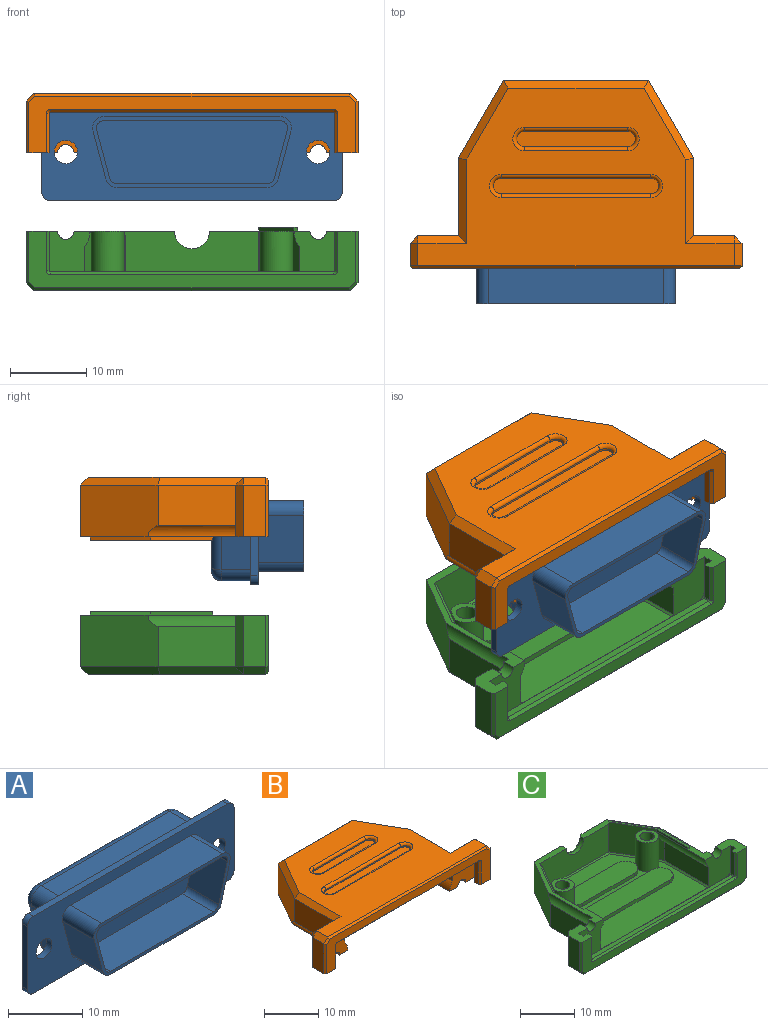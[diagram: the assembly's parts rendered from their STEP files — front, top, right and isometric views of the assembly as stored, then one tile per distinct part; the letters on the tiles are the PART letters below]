
ASSEMBLY  parts=3 mates=2
PART A: 47 faces, bbox 39.4x12.1x12.7 mm
  f0: plane 39.37x12.7mm, normal (0,1,0), area 180.2mm2, adj f2,f3,f4,f5,f6,f7,f8,f9
  f1: plane 39.37x12.7mm, normal (0,-1,0), area 260mm2, adj f2,f3,f4,f5,f6,f7,f8,f9
  f2: plane 10.41x1.02mm, normal (1,0,0), area 10.6mm2, adj f0,f1,f3,f11
  f3: cylinder r=1.14mm len=1.14mm, axis (0,-1,0), area 1.8mm2, adj f0,f1,f2,f4
  f4: plane 37.08x1.02mm, normal (0,0,1), area 37.7mm2, adj f0,f1,f3,f5
  f5: cylinder r=1.14mm len=1.14mm, axis (0,-1,0), area 1.8mm2, adj f0,f1,f4,f6
  f6: plane 10.41x1.02mm, normal (-1,0,0), area 10.6mm2, adj f0,f1,f5,f7
  f7: cylinder r=1.14mm len=1.14mm, axis (0,-1,0), area 1.8mm2, adj f0,f1,f6,f8
  f8: plane 37.08x1.02mm, normal (0,0,-1), area 37.7mm2, adj f0,f1,f7,f11
  f9: cylinder r=1.52mm len=3.05mm, axis (0,-1,0), area 9.7mm2, adj f0,f1
  f10: cylinder r=1.52mm len=3.05mm, axis (0,-1,0), area 9.7mm2, adj f0,f1
  f11: cylinder r=1.14mm len=1.14mm, axis (0,-1,0), area 1.8mm2, adj f0,f1,f2,f8
  f12: plane 6.22x5.97mm, normal (0.97,0,-0.26), area 38.5mm2, adj f1,f13,f27,f28
  f13: cylinder r=1.52mm len=5.97mm, axis (0,1,0), area 16.7mm2, adj f1,f12,f14,f28
  f14: plane 22.95x5.97mm, normal (0,0,1), area 137mm2, adj f1,f13,f15,f28
  f15: cylinder r=1.52mm len=5.97mm, axis (0,1,0), area 16.7mm2, adj f1,f14,f16,f28
  f16: plane 6.22x5.97mm, normal (-0.97,0,-0.26), area 38.5mm2, adj f1,f15,f17,f28
  f17: cylinder r=1.52mm len=5.97mm, axis (0,1,0), area 11.9mm2, adj f1,f16,f18,f28
  f18: plane 19.62x5.97mm, normal (0,0,-1), area 117.1mm2, adj f1,f17,f27,f28
  f19: cylinder r=1.02mm len=5.97mm, axis (0,1,0), area 11.1mm2, adj f20,f26,f28,f29
  f20: plane 6.22x5.97mm, normal (-0.97,0,0.26), area 38.5mm2, adj f19,f21,f28,f29
  f21: cylinder r=1.02mm len=5.97mm, axis (0,1,0), area 7.9mm2, adj f20,f22,f28,f29
  f22: plane 19.62x5.97mm, normal (0,0,1), area 117.1mm2, adj f21,f23,f28,f29
  f23: cylinder r=1.02mm len=5.97mm, axis (0,1,0), area 7.9mm2, adj f22,f24,f28,f29
  f24: plane 6.22x5.97mm, normal (0.97,0,0.26), area 38.5mm2, adj f23,f25,f28,f29
  f25: cylinder r=1.02mm len=5.97mm, axis (0,1,0), area 11.1mm2, adj f24,f26,f28,f29
  f26: plane 22.95x5.97mm, normal (0,0,-1), area 137mm2, adj f19,f25,f28,f29
  f27: cylinder r=1.52mm len=5.97mm, axis (0,1,0), area 11.9mm2, adj f1,f12,f18,f28
  f28: plane 26x9.27mm, normal (0,-1,0), area 32.2mm2, adj f12,f13,f14,f15,f16,f17,f18,f19
  f29: plane 24.98x8.26mm, normal (0,-1,0), area 192mm2, adj f19,f20,f21,f22,f23,f24,f25,f26
  f30: plane 7.87x3.81mm, normal (-0.97,0,-0.26), area 31.1mm2, adj f0,f31,f37,f42
  f31: cylinder r=1.91mm len=3.81mm, axis (0,-1,0), area 13.3mm2, adj f0,f30,f32,f40
  f32: plane 24.5x3.81mm, normal (0,0,1), area 93.3mm2, adj f0,f31,f33,f39
  f33: cylinder r=1.91mm len=3.81mm, axis (0,-1,0), area 13.3mm2, adj f0,f32,f34,f41
  f34: plane 7.87x3.81mm, normal (0.97,0,-0.26), area 31.1mm2, adj f0,f33,f35,f43
  f35: cylinder r=1.91mm len=3.81mm, axis (0,-1,0), area 9.5mm2, adj f0,f34,f36,f45
  f36: plane 20.28x3.81mm, normal (0,0,-1), area 77.3mm2, adj f0,f35,f37,f46
  f37: cylinder r=1.91mm len=3.81mm, axis (0,-1,0), area 9.5mm2, adj f0,f30,f36,f44
  f38: plane 25.77x9.14mm, normal (0,1,0), area 216.3mm2, adj f39,f40,f41,f42,f43,f44,f45,f46
  f39: cylinder r=1.27mm len=24.5mm, axis (-1,0,0), area 48.9mm2, adj f32,f38,f40,f41
  f40: torus R=0.64mm, axis (0,1,0), area 5.3mm2, adj f31,f38,f39,f42
  f41: torus R=0.64mm, axis (0,1,0), area 5.3mm2, adj f33,f38,f39,f43
  f42: cylinder r=1.27mm len=8.2mm, axis (0.26,0,-0.97), area 16.3mm2, adj f30,f38,f40,f44
  f43: cylinder r=1.27mm len=8.2mm, axis (0.26,0,0.97), area 16.3mm2, adj f34,f38,f41,f45
  f44: torus R=0.64mm, axis (0,1,0), area 3.8mm2, adj f37,f38,f42,f46
  f45: torus R=0.64mm, axis (0,1,0), area 3.8mm2, adj f35,f38,f43,f46
  f46: cylinder r=1.27mm len=20.28mm, axis (1,0,0), area 40.5mm2, adj f36,f38,f44,f45
PART B: 123 faces, bbox 43.4x24.6x8.3 mm
  f0: cone r=0mm half-angle=59deg, axis (0,0,-1), area 3.6mm2, adj f117,f122
  f1: cone r=0mm half-angle=59deg, axis (0,0,-1), area 3.6mm2, adj f118,f120
  f2: plane 22.1x13.14mm, normal (0,0,-1), area 30.9mm2, adj f3,f4,f17,f22,f60,f63,f76,f83
  f3: plane 39.88x6.6mm, normal (0,-1,0), area 77.1mm2, adj f2,f8,f10,f13,f14,f15,f27,f28
  f4: plane 18.99x6.78mm, normal (0,1,0), area 116.5mm2, adj f2,f13,f21,f22,f43,f116
  f5: plane 5.75x1.53mm, normal (-0.87,-0.5,0), area 8.8mm2, adj f8,f11,f75,f95,f106
  f6: plane 4.32x4.32mm, normal (0,0,-1), area 8.7mm2, adj f95,f102,f118
  f7: plane 5.94x5.75mm, normal (-0.87,-0.5,0), area 39.4mm2, adj f76,f81,f95,f106
  f8: cylinder r=3.17mm len=12.83mm, axis (0,-1,0), area 23.7mm2, adj f3,f5,f13,f75,f103,f106
  f9: plane 4.32x4.32mm, normal (0,0,-1), area 8.7mm2, adj f77,f94,f117
  f10: plane 27.63x20.56mm, normal (0,0,-1), area 309.5mm2, adj f3,f11,f12,f78,f79,f80,f81,f82
  f11: plane 1.6x0.92mm, normal (-0.61,-0.35,-0.71), area 0.6mm2, adj f5,f10,f82,f95
  f12: plane 1.6x0.92mm, normal (0.61,-0.35,-0.71), area 0.6mm2, adj f10,f77,f78,f94
  f13: plane 22.1x13.14mm, normal (0,0,-1), area 30.9mm2, adj f3,f4,f8,f16,f21,f61,f62,f76
  f14: plane 4.32x4.13mm, normal (0,0,-1), area 12.8mm2, adj f3,f17,f19,f23,f24,f27,f32,f38
  f15: plane 4.32x4.13mm, normal (0,0,-1), area 12.8mm2, adj f3,f16,f19,f24,f25,f28,f33,f49
  f16: plane 6.78x6.1mm, normal (0,1,0), area 35.2mm2, adj f13,f15,f20,f47,f49,f61,f62
  f17: plane 6.78x6.1mm, normal (0,1,0), area 35.2mm2, adj f2,f14,f18,f38,f40,f60,f63
  f18: plane 10.16x5.26mm, normal (-1,0,0), area 53.5mm2, adj f17,f22,f41,f60
  f19: plane 39.88x6.6mm, normal (0,1,0), area 63.4mm2, adj f14,f15,f27,f28,f29,f30,f31,f32
  f20: plane 10.16x5.26mm, normal (1,0,0), area 53.5mm2, adj f16,f21,f45,f61
  f21: plane 10.16x6.78mm, normal (0.87,0.5,0), area 78mm2, adj f4,f13,f20,f44,f61
  f22: plane 10.16x6.78mm, normal (-0.87,0.5,0), area 78mm2, adj f2,f4,f18,f42,f60
  f23: plane 6.78x2.92mm, normal (-1,0,0), area 19.8mm2, adj f14,f37,f38,f59
  f24: plane 42.67x7.42mm, normal (0,-1,0), area 98.2mm2, adj f14,f15,f50,f51,f52,f53,f54,f55
  f25: plane 6.78x2.92mm, normal (1,0,0), area 19.8mm2, adj f15,f46,f49,f55
  f26: plane 41.4x23.24mm, normal (0,0,1), area 537.1mm2, adj f37,f40,f41,f42,f43,f44,f45,f46
  f27: plane 5.21x1.27mm, normal (1,0,0), area 6.6mm2, adj f3,f14,f19,f31
  f28: plane 5.21x1.27mm, normal (-1,0,0), area 6.6mm2, adj f3,f15,f19,f29
  f29: cylinder r=1.4mm len=1.4mm, axis (0,-1,0), area 2.8mm2, adj f3,f19,f28,f30
  f30: plane 37.08x1.27mm, normal (0,0,-1), area 47.1mm2, adj f3,f19,f29,f31
  f31: cylinder r=1.4mm len=1.4mm, axis (0,-1,0), area 2.8mm2, adj f3,f19,f27,f30
  f32: plane 5.21x0.89mm, normal (1,0,0), area 4.6mm2, adj f14,f19,f36,f54
  f33: plane 5.21x0.89mm, normal (-1,0,0), area 4.6mm2, adj f15,f19,f34,f50
  f34: cylinder r=0.13mm len=0.89mm, axis (0,1,0), area 0.2mm2, adj f19,f33,f35,f51
  f35: plane 37.08x0.89mm, normal (0,0,-1), area 33mm2, adj f19,f34,f36,f52
  f36: cylinder r=0.13mm len=0.89mm, axis (0,1,0), area 0.2mm2, adj f19,f32,f35,f53
  f37: plane 2.92x1.02mm, normal (-0.71,0,0.71), area 4.2mm2, adj f23,f26,f39,f58
  f38: plane 6.78x1.02mm, normal (-0.71,0.71,0), area 9.7mm2, adj f14,f17,f23,f39
  f39: plane 1.02x1.02mm, normal (-0.58,0.58,0.58), area 0.9mm2, adj f37,f38,f40
  f40: plane 6.36x1.02mm, normal (0,0.71,0.71), area 8.4mm2, adj f17,f26,f39,f41
  f41: plane 11.18x1.02mm, normal (-0.71,0,0.71), area 15.1mm2, adj f18,f26,f40,f42
  f42: plane 10.43x6.45mm, normal (-0.61,0.35,0.71), area 16.2mm2, adj f22,f26,f41,f43
  f43: plane 18.99x1.02mm, normal (0,0.71,0.71), area 26.4mm2, adj f4,f26,f42,f44
  f44: plane 10.43x6.45mm, normal (0.61,0.35,0.71), area 16.2mm2, adj f21,f26,f43,f45
  f45: plane 11.18x1.02mm, normal (0.71,0,0.71), area 15.1mm2, adj f20,f26,f44,f47
  f46: plane 2.92x1.02mm, normal (0.71,0,0.71), area 4.2mm2, adj f25,f26,f48,f56
  f47: plane 6.36x1.02mm, normal (0,0.71,0.71), area 8.4mm2, adj f16,f26,f45,f48
  f48: plane 1.02x1.02mm, normal (0.58,0.58,0.58), area 0.9mm2, adj f46,f47,f49
  f49: plane 6.78x1.02mm, normal (0.71,0.71,0), area 9.7mm2, adj f15,f16,f25,f48
  f50: plane 5.21x0.38mm, normal (-0.71,-0.71,0), area 2.8mm2, adj f15,f24,f33,f51
  f51: cone r=0.51mm half-angle=45deg, axis (0,-1,0), area 0.3mm2, adj f24,f34,f50,f52
  f52: plane 37.08x0.38mm, normal (0,-0.71,-0.71), area 20mm2, adj f24,f35,f51,f53
  f53: cone r=0.51mm half-angle=45deg, axis (0,-1,0), area 0.3mm2, adj f24,f36,f52,f54
  f54: plane 5.21x0.38mm, normal (0.71,-0.71,0), area 2.8mm2, adj f14,f24,f32,f53
  f55: plane 6.78x0.38mm, normal (0.71,-0.71,0), area 3.6mm2, adj f15,f24,f25,f56
  f56: plane 1.17x1.17mm, normal (0.5,-0.71,0.5), area 0.7mm2, adj f24,f46,f55,f57
  f57: plane 41.4x0.38mm, normal (0,-0.71,0.71), area 22.2mm2, adj f24,f26,f56,f58
  f58: plane 1.17x1.17mm, normal (-0.5,-0.71,0.5), area 0.7mm2, adj f24,f37,f57,f59
  f59: plane 6.78x0.38mm, normal (-0.71,-0.71,0), area 3.6mm2, adj f14,f23,f24,f58
  f60: cylinder r=1.91mm len=11.47mm, axis (0,-1,0), area 19.4mm2, adj f2,f17,f18,f22
  f61: cylinder r=1.91mm len=11.47mm, axis (0,-1,0), area 19.4mm2, adj f13,f16,f20,f21
  f62: cylinder r=1.08mm len=2.16mm, axis (0,1,0), area 6mm2, adj f3,f13,f15,f16
  f63: cylinder r=1.08mm len=2.16mm, axis (0,1,0), area 6mm2, adj f2,f3,f14,f17
  f64: plane 19.62x0.25mm, normal (0,-1,0), area 5mm2, adj f65,f67,f68,f108
  f65: cylinder r=1.02mm len=2.03mm, axis (0,0,1), area 0.8mm2, adj f64,f66,f68,f109
  f66: plane 19.62x0.25mm, normal (0,1,0), area 5mm2, adj f65,f67,f68,f111
  f67: cylinder r=1.02mm len=2.03mm, axis (0,0,1), area 0.8mm2, adj f64,f66,f68,f110
  f68: plane 21.65x2.03mm, normal (0,0,1), area 43.1mm2, adj f64,f65,f66,f67
  f69: plane 13.5x0.25mm, normal (0,-1,0), area 3.4mm2, adj f70,f72,f73,f112
  f70: cylinder r=1.02mm len=2.03mm, axis (0,0,1), area 0.8mm2, adj f69,f71,f73,f113
  f71: plane 13.5x0.25mm, normal (0,1,0), area 3.4mm2, adj f70,f72,f73,f115
  f72: cylinder r=1.02mm len=2.03mm, axis (0,0,1), area 0.8mm2, adj f69,f71,f73,f114
  f73: plane 15.53x2.03mm, normal (0,0,1), area 30.7mm2, adj f69,f70,f71,f72
  f74: plane 11.6x4.2mm, normal (1,0,0), area 48.7mm2, adj f3,f77,f78,f83
  f75: plane 11.6x4.2mm, normal (-1,0,0), area 48.7mm2, adj f3,f5,f8,f82
  f76: plane 18.03x6.26mm, normal (0,-1,0), area 101.7mm2, adj f2,f7,f13,f77,f80,f104,f106,f107
  f77: plane 9.23x6.76mm, normal (0.87,-0.5,0), area 56.5mm2, adj f9,f12,f74,f76,f79,f83,f94,f96
  f78: plane 11.6x0.27mm, normal (0.71,0,-0.71), area 4.4mm2, adj f3,f10,f12,f74
  f79: plane 5.94x3.59mm, normal (0.61,-0.35,-0.71), area 2.5mm2, adj f10,f77,f80,f94
  f80: plane 17.52x0.27mm, normal (0,-0.71,-0.71), area 6.7mm2, adj f10,f76,f79,f81
  f81: plane 5.94x3.59mm, normal (-0.61,-0.35,-0.71), area 2.5mm2, adj f7,f10,f80,f95
  f82: plane 11.6x0.27mm, normal (-0.71,0,-0.71), area 4.4mm2, adj f3,f10,f11,f75
  f83: cylinder r=3.17mm len=12.9mm, axis (0,-1,0), area 27.8mm2, adj f2,f3,f74,f77,f96
  f84: plane 19.62x0.76mm, normal (0,1,0), area 15mm2, adj f10,f85,f87,f88
  f85: cylinder r=2.29mm len=4.57mm, axis (0,0,1), area 5.5mm2, adj f10,f84,f86,f88
  f86: plane 19.62x0.76mm, normal (0,-1,0), area 15mm2, adj f10,f85,f87,f88
  f87: cylinder r=2.29mm len=4.57mm, axis (0,0,1), area 5.5mm2, adj f10,f84,f86,f88
  f88: plane 24.19x4.57mm, normal (0,0,-1), area 106.1mm2, adj f84,f85,f86,f87
  f89: plane 13.5x0.76mm, normal (0,1,0), area 10.3mm2, adj f10,f90,f92,f93
  f90: cylinder r=2.29mm len=4.57mm, axis (0,0,1), area 5.5mm2, adj f10,f89,f91,f93
  f91: plane 13.5x0.76mm, normal (0,-1,0), area 10.3mm2, adj f10,f90,f92,f93
  f92: cylinder r=2.29mm len=4.57mm, axis (0,0,1), area 5.5mm2, adj f10,f89,f91,f93
  f93: plane 18.07x4.57mm, normal (0,0,-1), area 78.1mm2, adj f89,f90,f91,f92
  f94: cylinder r=2.16mm len=6.53mm, axis (0,0,-1), area 74.6mm2, adj f9,f10,f12,f77,f79
  f95: cylinder r=2.16mm len=6.53mm, axis (0,0,-1), area 74.6mm2, adj f5,f6,f7,f10,f11,f81,f102
  f96: plane 8.13x0.51mm, normal (1,0,0), area 4.1mm2, adj f77,f83,f97,f101
  f97: plane 0.51x0.51mm, normal (0,-1,0), area 0.3mm2, adj f2,f96,f98,f101
  f98: plane 8.13x0.51mm, normal (-1,0,0), area 4.1mm2, adj f2,f97,f99,f101
  f99: plane 7.92x4.57mm, normal (-0.87,0.5,0), area 4.6mm2, adj f2,f98,f100,f101
  f100: plane 0.51x0.51mm, normal (0,1,0), area 0.3mm2, adj f2,f77,f99,f101
  f101: plane 16.05x5.08mm, normal (0,0,-1), area 8.2mm2, adj f77,f96,f97,f98,f99,f100
  f102: plane 1.76x1.02mm, normal (0.87,0.5,0), area 1mm2, adj f6,f95,f106
  f103: plane 0.51x0.51mm, normal (0,1,0), area 0.3mm2, adj f8,f13,f105,f106
  f104: plane 7.92x4.57mm, normal (-0.87,-0.5,0), area 4.6mm2, adj f13,f76,f105,f106
  f105: plane 8.13x0.51mm, normal (-1,0,0), area 4.1mm2, adj f13,f103,f104,f106
  f106: plane 16.05x5.08mm, normal (0,0,-1), area 7.8mm2, adj f5,f7,f8,f76,f102,f103,f104,f105
  f107: cylinder r=2.29mm len=4.57mm, axis (0,1,0), area 5.5mm2, adj f2,f13,f76,f116
  f108: cylinder r=0.51mm len=19.62mm, axis (1,0,0), area 15.7mm2, adj f26,f64,f109,f110
  f109: torus R=1.52mm, axis (0,0,1), area 3mm2, adj f26,f65,f108,f111
  f110: torus R=1.52mm, axis (0,0,1), area 3mm2, adj f26,f67,f108,f111
  f111: cylinder r=0.51mm len=19.62mm, axis (-1,0,0), area 15.7mm2, adj f26,f66,f109,f110
  f112: cylinder r=0.51mm len=13.5mm, axis (1,0,0), area 10.8mm2, adj f26,f69,f113,f114
  f113: torus R=1.52mm, axis (0,0,1), area 3mm2, adj f26,f70,f112,f115
  f114: torus R=1.52mm, axis (0,0,1), area 3mm2, adj f26,f72,f112,f115
  f115: cylinder r=0.51mm len=13.5mm, axis (-1,0,0), area 10.8mm2, adj f26,f71,f113,f114
  f116: torus R=2.79mm, axis (0,-1,0), area 6.2mm2, adj f2,f4,f13,f107
  f117: cylinder r=1.33mm len=2.67mm, axis (0,0,-1), area 2.8mm2, adj f0,f9
  f118: cylinder r=1.33mm len=2.67mm, axis (0,0,-1), area 2.8mm2, adj f1,f6
  f119: cone r=0mm half-angle=59deg, axis (0,0,-1), area 2.9mm2, adj f120
  f120: cylinder r=0.89mm len=5.75mm, axis (0,0,-1), area 32.1mm2, adj f1,f119
  f121: cone r=0mm half-angle=59deg, axis (0,0,-1), area 2.9mm2, adj f122
  f122: cylinder r=0.89mm len=5.75mm, axis (0,0,-1), area 32.1mm2, adj f0,f121
PART C: 121 faces, bbox 43.4x24.6x8.3 mm
  f0: plane 22.1x13.14mm, normal (0,0,1), area 30.9mm2, adj f1,f2,f15,f20,f58,f61,f74,f81
  f1: plane 39.88x6.6mm, normal (0,-1,0), area 77.1mm2, adj f0,f6,f8,f11,f12,f13,f25,f26
  f2: plane 18.99x6.78mm, normal (0,1,0), area 116.5mm2, adj f0,f11,f19,f20,f41,f114
  f3: plane 5.75x1.53mm, normal (0.87,-0.5,0), area 8.8mm2, adj f6,f9,f73,f93,f104
  f4: plane 4.32x4.32mm, normal (0,0,1), area 8.7mm2, adj f93,f100,f118
  f5: plane 5.94x5.75mm, normal (0.87,-0.5,0), area 39.4mm2, adj f74,f79,f93,f104
  f6: cylinder r=3.17mm len=12.83mm, axis (0,-1,0), area 23.7mm2, adj f1,f3,f11,f73,f101,f104
  f7: plane 4.32x4.32mm, normal (0,0,1), area 8.7mm2, adj f75,f92,f115
  f8: plane 27.63x20.56mm, normal (0,0,1), area 309.5mm2, adj f1,f9,f10,f76,f77,f78,f79,f80
  f9: plane 1.6x0.92mm, normal (0.61,-0.35,0.71), area 0.6mm2, adj f3,f8,f80,f93
  f10: plane 1.6x0.92mm, normal (-0.61,-0.35,0.71), area 0.6mm2, adj f8,f75,f76,f92
  f11: plane 22.1x13.14mm, normal (0,0,1), area 30.9mm2, adj f1,f2,f6,f14,f19,f59,f60,f74
  f12: plane 4.32x4.13mm, normal (0,0,1), area 12.8mm2, adj f1,f15,f17,f21,f22,f25,f30,f36
  f13: plane 4.32x4.13mm, normal (0,0,1), area 12.8mm2, adj f1,f14,f17,f22,f23,f26,f31,f47
  f14: plane 6.78x6.1mm, normal (0,1,0), area 35.2mm2, adj f11,f13,f18,f45,f47,f59,f60
  f15: plane 6.78x6.1mm, normal (0,1,0), area 35.2mm2, adj f0,f12,f16,f36,f38,f58,f61
  f16: plane 10.16x5.26mm, normal (1,0,0), area 53.5mm2, adj f15,f20,f39,f58
  f17: plane 39.88x6.6mm, normal (0,1,0), area 63.4mm2, adj f12,f13,f25,f26,f27,f28,f29,f30
  f18: plane 10.16x5.26mm, normal (-1,0,0), area 53.5mm2, adj f14,f19,f43,f59
  f19: plane 10.16x6.78mm, normal (-0.87,0.5,0), area 78mm2, adj f2,f11,f18,f42,f59
  f20: plane 10.16x6.78mm, normal (0.87,0.5,0), area 78mm2, adj f0,f2,f16,f40,f58
  f21: plane 6.78x2.92mm, normal (1,0,0), area 19.8mm2, adj f12,f35,f36,f57
  f22: plane 42.67x7.42mm, normal (0,-1,0), area 98.2mm2, adj f12,f13,f48,f49,f50,f51,f52,f53
  f23: plane 6.78x2.92mm, normal (-1,0,0), area 19.8mm2, adj f13,f44,f47,f53
  f24: plane 41.4x23.24mm, normal (0,0,-1), area 512.8mm2, adj f35,f38,f39,f40,f41,f42,f43,f44
  f25: plane 5.21x1.27mm, normal (-1,0,0), area 6.6mm2, adj f1,f12,f17,f29
  f26: plane 5.21x1.27mm, normal (1,0,0), area 6.6mm2, adj f1,f13,f17,f27
  f27: cylinder r=1.4mm len=1.4mm, axis (0,-1,0), area 2.8mm2, adj f1,f17,f26,f28
  f28: plane 37.08x1.27mm, normal (0,0,1), area 47.1mm2, adj f1,f17,f27,f29
  f29: cylinder r=1.4mm len=1.4mm, axis (0,-1,0), area 2.8mm2, adj f1,f17,f25,f28
  f30: plane 5.21x0.89mm, normal (-1,0,0), area 4.6mm2, adj f12,f17,f34,f52
  f31: plane 5.21x0.89mm, normal (1,0,0), area 4.6mm2, adj f13,f17,f32,f48
  f32: cylinder r=0.13mm len=0.89mm, axis (0,1,0), area 0.2mm2, adj f17,f31,f33,f49
  f33: plane 37.08x0.89mm, normal (0,0,1), area 33mm2, adj f17,f32,f34,f50
  f34: cylinder r=0.13mm len=0.89mm, axis (0,1,0), area 0.2mm2, adj f17,f30,f33,f51
  f35: plane 2.92x1.02mm, normal (0.71,0,-0.71), area 4.2mm2, adj f21,f24,f37,f56
  f36: plane 6.78x1.02mm, normal (0.71,0.71,0), area 9.7mm2, adj f12,f15,f21,f37
  f37: plane 1.02x1.02mm, normal (0.58,0.58,-0.58), area 0.9mm2, adj f35,f36,f38
  f38: plane 6.36x1.02mm, normal (0,0.71,-0.71), area 8.4mm2, adj f15,f24,f37,f39
  f39: plane 11.18x1.02mm, normal (0.71,0,-0.71), area 15.1mm2, adj f16,f24,f38,f40
  f40: plane 10.43x6.45mm, normal (0.61,0.35,-0.71), area 16.2mm2, adj f20,f24,f39,f41
  f41: plane 18.99x1.02mm, normal (0,0.71,-0.71), area 26.4mm2, adj f2,f24,f40,f42
  f42: plane 10.43x6.45mm, normal (-0.61,0.35,-0.71), area 16.2mm2, adj f19,f24,f41,f43
  f43: plane 11.18x1.02mm, normal (-0.71,0,-0.71), area 15.1mm2, adj f18,f24,f42,f45
  f44: plane 2.92x1.02mm, normal (-0.71,0,-0.71), area 4.2mm2, adj f23,f24,f46,f54
  f45: plane 6.36x1.02mm, normal (0,0.71,-0.71), area 8.4mm2, adj f14,f24,f43,f46
  f46: plane 1.02x1.02mm, normal (-0.58,0.58,-0.58), area 0.9mm2, adj f44,f45,f47
  f47: plane 6.78x1.02mm, normal (-0.71,0.71,0), area 9.7mm2, adj f13,f14,f23,f46
  f48: plane 5.21x0.38mm, normal (0.71,-0.71,0), area 2.8mm2, adj f13,f22,f31,f49
  f49: cone r=0.51mm half-angle=45deg, axis (0,-1,0), area 0.3mm2, adj f22,f32,f48,f50
  f50: plane 37.08x0.38mm, normal (0,-0.71,0.71), area 20mm2, adj f22,f33,f49,f51
  f51: cone r=0.51mm half-angle=45deg, axis (0,-1,0), area 0.3mm2, adj f22,f34,f50,f52
  f52: plane 5.21x0.38mm, normal (-0.71,-0.71,0), area 2.8mm2, adj f12,f22,f30,f51
  f53: plane 6.78x0.38mm, normal (-0.71,-0.71,0), area 3.6mm2, adj f13,f22,f23,f54
  f54: plane 1.17x1.17mm, normal (-0.5,-0.71,-0.5), area 0.7mm2, adj f22,f44,f53,f55
  f55: plane 41.4x0.38mm, normal (0,-0.71,-0.71), area 22.2mm2, adj f22,f24,f54,f56
  f56: plane 1.17x1.17mm, normal (0.5,-0.71,-0.5), area 0.7mm2, adj f22,f35,f55,f57
  f57: plane 6.78x0.38mm, normal (0.71,-0.71,0), area 3.6mm2, adj f12,f21,f22,f56
  f58: cylinder r=1.91mm len=11.47mm, axis (0,-1,0), area 19.4mm2, adj f0,f15,f16,f20
  f59: cylinder r=1.91mm len=11.47mm, axis (0,-1,0), area 19.4mm2, adj f11,f14,f18,f19
  f60: cylinder r=1.08mm len=2.16mm, axis (0,1,0), area 6mm2, adj f1,f11,f13,f14
  f61: cylinder r=1.08mm len=2.16mm, axis (0,1,0), area 6mm2, adj f0,f1,f12,f15
  f62: plane 19.62x0.25mm, normal (0,-1,0), area 5mm2, adj f63,f65,f66,f106
  f63: cylinder r=1.02mm len=2.03mm, axis (0,0,-1), area 0.8mm2, adj f62,f64,f66,f107
  f64: plane 19.62x0.25mm, normal (0,1,0), area 5mm2, adj f63,f65,f66,f109
  f65: cylinder r=1.02mm len=2.03mm, axis (0,0,-1), area 0.8mm2, adj f62,f64,f66,f108
  f66: plane 21.65x2.03mm, normal (0,0,-1), area 43.1mm2, adj f62,f63,f64,f65
  f67: plane 13.5x0.25mm, normal (0,-1,0), area 3.4mm2, adj f68,f70,f71,f110
  f68: cylinder r=1.02mm len=2.03mm, axis (0,0,-1), area 0.8mm2, adj f67,f69,f71,f111
  f69: plane 13.5x0.25mm, normal (0,1,0), area 3.4mm2, adj f68,f70,f71,f113
  f70: cylinder r=1.02mm len=2.03mm, axis (0,0,-1), area 0.8mm2, adj f67,f69,f71,f112
  f71: plane 15.53x2.03mm, normal (0,0,-1), area 30.7mm2, adj f67,f68,f69,f70
  f72: plane 11.6x4.2mm, normal (-1,0,0), area 48.7mm2, adj f1,f75,f76,f81
  f73: plane 11.6x4.2mm, normal (1,0,0), area 48.7mm2, adj f1,f3,f6,f80
  f74: plane 18.03x6.26mm, normal (0,-1,0), area 101.7mm2, adj f0,f5,f11,f75,f78,f102,f104,f105
  f75: plane 9.23x6.76mm, normal (-0.87,-0.5,0), area 56.5mm2, adj f7,f10,f72,f74,f77,f81,f92,f94
  f76: plane 11.6x0.27mm, normal (-0.71,0,0.71), area 4.4mm2, adj f1,f8,f10,f72
  f77: plane 5.94x3.59mm, normal (-0.61,-0.35,0.71), area 2.5mm2, adj f8,f75,f78,f92
  f78: plane 17.52x0.27mm, normal (0,-0.71,0.71), area 6.7mm2, adj f8,f74,f77,f79
  f79: plane 5.94x3.59mm, normal (0.61,-0.35,0.71), area 2.5mm2, adj f5,f8,f78,f93
  f80: plane 11.6x0.27mm, normal (0.71,0,0.71), area 4.4mm2, adj f1,f8,f9,f73
  f81: cylinder r=3.17mm len=12.9mm, axis (0,-1,0), area 27.8mm2, adj f0,f1,f72,f75,f94
  f82: plane 19.62x0.76mm, normal (0,1,0), area 15mm2, adj f8,f83,f85,f86
  f83: cylinder r=2.29mm len=4.57mm, axis (0,0,-1), area 5.5mm2, adj f8,f82,f84,f86
  f84: plane 19.62x0.76mm, normal (0,-1,0), area 15mm2, adj f8,f83,f85,f86
  f85: cylinder r=2.29mm len=4.57mm, axis (0,0,-1), area 5.5mm2, adj f8,f82,f84,f86
  f86: plane 24.19x4.57mm, normal (0,0,1), area 106.1mm2, adj f82,f83,f84,f85
  f87: plane 13.5x0.76mm, normal (0,1,0), area 10.3mm2, adj f8,f88,f90,f91
  f88: cylinder r=2.29mm len=4.57mm, axis (0,0,-1), area 5.5mm2, adj f8,f87,f89,f91
  f89: plane 13.5x0.76mm, normal (0,-1,0), area 10.3mm2, adj f8,f88,f90,f91
  f90: cylinder r=2.29mm len=4.57mm, axis (0,0,-1), area 5.5mm2, adj f8,f87,f89,f91
  f91: plane 18.07x4.57mm, normal (0,0,1), area 78.1mm2, adj f87,f88,f89,f90
  f92: cylinder r=2.16mm len=6.53mm, axis (0,0,1), area 74.6mm2, adj f7,f8,f10,f75,f77
  f93: cylinder r=2.16mm len=6.53mm, axis (0,0,1), area 74.6mm2, adj f3,f4,f5,f8,f9,f79,f100
  f94: plane 8.13x0.51mm, normal (-1,0,0), area 4.1mm2, adj f75,f81,f95,f99
  f95: plane 0.51x0.51mm, normal (0,-1,0), area 0.3mm2, adj f0,f94,f96,f99
  f96: plane 8.13x0.51mm, normal (1,0,0), area 4.1mm2, adj f0,f95,f97,f99
  f97: plane 7.92x4.57mm, normal (0.87,0.5,0), area 4.6mm2, adj f0,f96,f98,f99
  f98: plane 0.51x0.51mm, normal (0,1,0), area 0.3mm2, adj f0,f75,f97,f99
  f99: plane 16.05x5.08mm, normal (0,0,1), area 8.2mm2, adj f75,f94,f95,f96,f97,f98
  f100: plane 1.76x1.02mm, normal (-0.87,0.5,0), area 1mm2, adj f4,f93,f104
  f101: plane 0.51x0.51mm, normal (0,1,0), area 0.3mm2, adj f6,f11,f103,f104
  f102: plane 7.92x4.57mm, normal (0.87,-0.5,0), area 4.6mm2, adj f11,f74,f103,f104
  f103: plane 8.13x0.51mm, normal (1,0,0), area 4.1mm2, adj f11,f101,f102,f104
  f104: plane 16.05x5.08mm, normal (0,0,1), area 7.8mm2, adj f3,f5,f6,f74,f100,f101,f102,f103
  f105: cylinder r=2.29mm len=4.57mm, axis (0,1,0), area 5.5mm2, adj f0,f11,f74,f114
  f106: cylinder r=0.51mm len=19.62mm, axis (-1,0,0), area 15.7mm2, adj f24,f62,f107,f108
  f107: torus R=1.52mm, axis (0,0,-1), area 3mm2, adj f24,f63,f106,f109
  f108: torus R=1.52mm, axis (0,0,-1), area 3mm2, adj f24,f65,f106,f109
  f109: cylinder r=0.51mm len=19.62mm, axis (1,0,0), area 15.7mm2, adj f24,f64,f107,f108
  f110: cylinder r=0.51mm len=13.5mm, axis (-1,0,0), area 10.8mm2, adj f24,f67,f111,f112
  f111: torus R=1.52mm, axis (0,0,-1), area 3mm2, adj f24,f68,f110,f113
  f112: torus R=1.52mm, axis (0,0,-1), area 3mm2, adj f24,f70,f110,f113
  f113: cylinder r=0.51mm len=13.5mm, axis (1,0,0), area 10.8mm2, adj f24,f69,f111,f112
  f114: torus R=2.79mm, axis (0,-1,0), area 6.2mm2, adj f0,f2,f11,f105
  f115: cylinder r=1.33mm len=6.53mm, axis (0,0,-1), area 54.7mm2, adj f7,f116
  f116: plane 3.94x3.94mm, normal (0,0,-1), area 6.6mm2, adj f115,f117
  f117: cylinder r=1.97mm len=3.94mm, axis (0,0,-1), area 15.7mm2, adj f24,f116
  f118: cylinder r=1.33mm len=6.53mm, axis (0,0,-1), area 54.7mm2, adj f4,f119
  f119: plane 3.94x3.94mm, normal (0,0,-1), area 6.6mm2, adj f118,f120
  f120: cylinder r=1.97mm len=3.94mm, axis (0,0,-1), area 15.7mm2, adj f24,f119
PLACE A t=(0,0.13,10.35)mm
PLACE B t=(0,0,10.24)mm
PLACE C at identity fixed
MATE slider C.f0 <-> B.f13  axis (0,0,1) through (9.49,23.37,0)mm
MATE slider C.f28 <-> A.f8  axis (0,0,1) through (0,0.64,-6.6)mm
